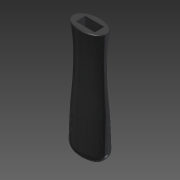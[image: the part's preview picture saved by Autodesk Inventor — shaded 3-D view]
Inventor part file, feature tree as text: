
AUTODESK INVENTOR PART (.ipt)
format: ipt  version: 2015 (Build 190159000, 159)  size: 337,408 bytes
history: native  units: mm
features: sketch x6, other x5, fillet x2, loft x1, extrude x1
ambient origin geometry x8: Origin, YZ Plane, XZ Plane, XY Plane, X Axis, Y Axis, Z Axis, Center Point
bodies: Body1 (feature_tree)
feature tree (15):
  other  "Bryła2"
  sketch  "Szkic1"
  other  "Płaszczyzna konstrukcyjna1"
  sketch  "Szkic4"
  other  "Płaszczyzna konstrukcyjna2"
  sketch  "Szkic5"
  other  "Płaszczyzna konstrukcyjna3"
  sketch  "Szkic6"
  other  "Płaszczyzna konstrukcyjna4"
  loft  "Wyciągnięcie złożone2"
  fillet  "Zaokrąglenie1"  Radius=5.0mm
  fillet  "Zaokrąglenie2"  Radius=9.0mm
  extrude  "Wyciągnięcie proste1"  Depth=5.5mm
  sketch  "Szkic7"
  sketch  "Szkic8"
